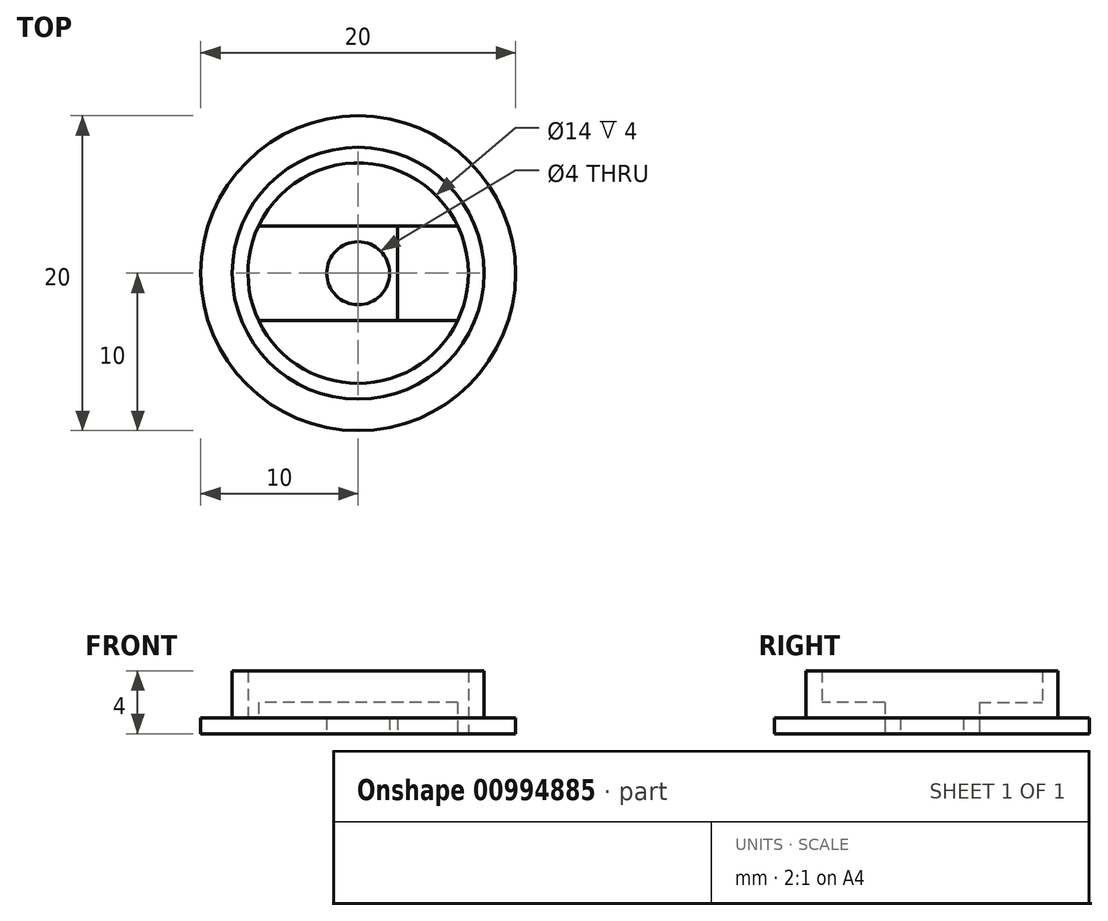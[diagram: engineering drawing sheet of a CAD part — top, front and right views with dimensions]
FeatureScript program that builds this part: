
annotation { "Feature Type Name" : "Feature", "Feature Type Description" : "" }
export const myFeature = defineFeature(function(context is Context, id is Id, definition is map)
    precondition{}
    {
        {
            var Q0;
            Q0=qCreatedBy(makeId("Top.planeOp"),FACE);
            var sketch = newSketch(context, id + "F0", { "sketchPlane" : qUnion([Q0])});
            skCircle(sketch, "E0", {"center": v(0, 0) * mm, "radius": 10 * mm});
            skCircle(sketch, "E1", {"center": v(0, 0) * mm, "radius": 8 * mm});
            skCircle(sketch, "E2", {"center": v(0, 0) * mm, "radius": 7 * mm});
            skCircle(sketch, "E3", {"center": v(0, 0) * mm, "radius": 2 * mm});
            skLineSegment(sketch, "E4", {"start": v(2.5, 6.54) * mm, "end": v(2.5, -6.54) * mm});
            skLineSegment(sketch, "E5", {"start": v(6.32, -3) * mm, "end": v(-6.32, -3) * mm});
            skLineSegment(sketch, "E6", {"start": v(6.32, 3) * mm, "end": v(-6.32, 3) * mm});
            skSolve(sketch);
        }
        {
            var Q0;
            Q0=makeQuery(id+"F0.imprint","IMPRINT",FACE,{"disambiguationData":[TD([[makeQuery(id+"F0.imprint","IMPRINT",EDGE,{"derivedFrom":sQuery(id+"F0.wireOp",EDGE,"E2")}),1.0]])]});
            var Q1;
            Q1=makeQuery(id+"F0.imprint","IMPRINT",FACE,{"disambiguationData":[TD([[makeQuery(id+"F0.imprint","IMPRINT",EDGE,{"derivedFrom":sQuery(id+"F0.wireOp",EDGE,"E1")}),1.0]])]});
            var Q2;
            Q2=makeQuery(id+"F0.imprint","IMPRINT",FACE,{"disambiguationData":[TD([[makeQuery(id+"F0.imprint","IMPRINT",EDGE,{"derivedFrom":sQuery(id+"F0.wireOp",EDGE,"E0")}),1.0]])]});
            var Q3;
            {var subQ0=sQuery(id+"F0.wireOp",EDGE,"E5");var subQ1=sQuery(id+"F0.wireOp",EDGE,"E2");var subQ2=makeQuery(id+"F0.imprint","INTERSECT",VERTEX,{"disambiguationData":[OD(0.0)],"derivedFrom":[subQ1,subQ0]});Q3=makeQuery(id+"F0.imprint","IMPRINT",FACE,{"disambiguationData":[TD([[makeQuery(id+"F0.imprint","IMPRINT",EDGE,{"disambiguationData":[TD([[subQ2,-1.0]])],"derivedFrom":subQ1}),1.0]])]});}
            var Q4;
            Q4=makeQuery(id+"F0.imprint","IMPRINT",FACE,{"disambiguationData":[TD([[makeQuery(id+"F0.imprint","IMPRINT",EDGE,{"derivedFrom":sQuery(id+"F0.wireOp",EDGE,"E3")}),-1.0]])]});
            extrude(context, id + "F1", {"entities" : qUnion([Q0, Q1, Q2, Q3, Q4]), "depth" : 1 * mm, "offsetDistance" : 25 * mm});
        }
        {
            var Q0;
            Q0=makeQuery(id+"F0.imprint","IMPRINT",FACE,{"disambiguationData":[TD([[makeQuery(id+"F0.imprint","IMPRINT",EDGE,{"derivedFrom":sQuery(id+"F0.wireOp",EDGE,"E1")}),1.0]])]});
            extrude(context, id + "F2", {"entities" : qUnion([Q0]), "operationType" : NewBodyOperationType.ADD, "depth" : 4 * mm, "offsetDistance" : 25 * mm});
        }
        {
            var Q0;
            {var subQ0=sQuery(id+"F0.wireOp",EDGE,"E4");var subQ1=sQuery(id+"F0.wireOp",EDGE,"E2");var subQ2=makeQuery(id+"F0.imprint","INTERSECT",VERTEX,{"disambiguationData":[OD(0.0)],"derivedFrom":[subQ1,subQ0]});Q0=makeQuery(id+"F0.imprint","IMPRINT",FACE,{"disambiguationData":[TD([[makeQuery(id+"F0.imprint","IMPRINT",EDGE,{"disambiguationData":[TD([[subQ2,-1.0]])],"derivedFrom":subQ1}),1.0]])]});}
            var Q1;
            {var subQ0=sQuery(id+"F0.wireOp",EDGE,"E4");var subQ1=sQuery(id+"F0.wireOp",EDGE,"E2");var subQ2=makeQuery(id+"F0.imprint","INTERSECT",VERTEX,{"disambiguationData":[OD(0.0)],"derivedFrom":[subQ1,subQ0]});Q1=makeQuery(id+"F0.imprint","IMPRINT",FACE,{"disambiguationData":[TD([[makeQuery(id+"F0.imprint","IMPRINT",EDGE,{"disambiguationData":[TD([[subQ2,1.0]])],"derivedFrom":subQ1}),1.0]])]});}
            var Q2;
            {var subQ0=sQuery(id+"F0.wireOp",EDGE,"E5");var subQ1=sQuery(id+"F0.wireOp",EDGE,"E2");var subQ2=makeQuery(id+"F0.imprint","INTERSECT",VERTEX,{"disambiguationData":[OD(0.0)],"derivedFrom":[subQ1,subQ0]});Q2=makeQuery(id+"F0.imprint","IMPRINT",FACE,{"disambiguationData":[TD([[makeQuery(id+"F0.imprint","IMPRINT",EDGE,{"disambiguationData":[TD([[subQ2,-1.0]])],"derivedFrom":subQ1}),1.0]])]});}
            var Q3;
            {var subQ0=sQuery(id+"F0.wireOp",EDGE,"E4");var subQ1=sQuery(id+"F0.wireOp",EDGE,"E2");var subQ2=makeQuery(id+"F0.imprint","INTERSECT",VERTEX,{"disambiguationData":[OD(1.0)],"derivedFrom":[subQ1,subQ0]});Q3=makeQuery(id+"F0.imprint","IMPRINT",FACE,{"disambiguationData":[TD([[makeQuery(id+"F0.imprint","IMPRINT",EDGE,{"disambiguationData":[TD([[subQ2,-1.0]])],"derivedFrom":subQ1}),1.0]])]});}
            var Q4;
            {var subQ0=sQuery(id+"F0.wireOp",EDGE,"E4");var subQ1=sQuery(id+"F0.wireOp",EDGE,"E2");var subQ2=makeQuery(id+"F0.imprint","INTERSECT",VERTEX,{"disambiguationData":[OD(1.0)],"derivedFrom":[subQ1,subQ0]});Q4=makeQuery(id+"F0.imprint","IMPRINT",FACE,{"disambiguationData":[TD([[makeQuery(id+"F0.imprint","IMPRINT",EDGE,{"disambiguationData":[TD([[subQ2,1.0]])],"derivedFrom":subQ1}),1.0]])]});}
            extrude(context, id + "F3", {"entities" : qUnion([Q0, Q1, Q2, Q3, Q4]), "operationType" : NewBodyOperationType.ADD, "depth" : 2 * mm, "offsetDistance" : 25 * mm});
        }
    });
